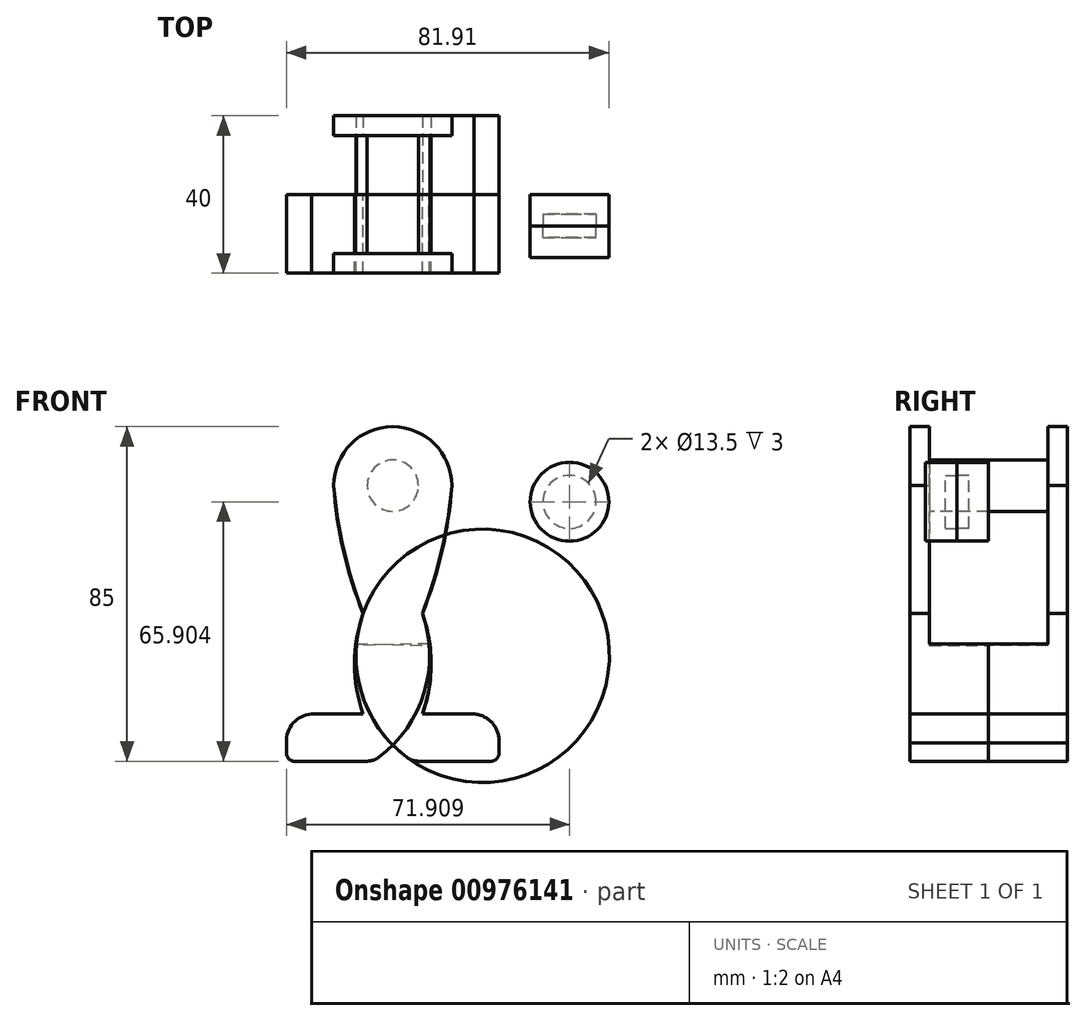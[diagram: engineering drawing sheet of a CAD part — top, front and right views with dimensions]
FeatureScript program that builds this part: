
annotation { "Feature Type Name" : "Feature", "Feature Type Description" : "" }
export const myFeature = defineFeature(function(context is Context, id is Id, definition is map)
    precondition{}
    {
        {
            var Q0;
            Q0=qCreatedBy(makeId("Front.planeOp"),FACE);
            var sketch = newSketch(context, id + "F0", { "sketchPlane" : qUnion([Q0])});
            skArc(sketch, "E0", {"start": v(14.72, 5.88) * mm, "mid": v(0.24, 23.76) * mm, "end": v(-14.8, 6.36) * mm});
            skLineSegment(sketch, "E1", {"start": v(-6.58, -61.23) * mm, "end": v(-25, -61.23) * mm});
            skPoint(sketch, "E2.visualSharp", {"position": v(0, -61.23) * mm});
            skLineSegment(sketch, "E3", {"start": v(-27, -59.23) * mm, "end": v(-27, -56.54) * mm});
            skLineSegment(sketch, "E4", {"start": v(-20.6, -49.23) * mm, "end": v(-7.5, -49.23) * mm});
            skArc(sketch, "E5", {"start": v(-15, 8.77) * mm, "mid": v(-12.53, -7.78) * mm, "end": v(-7.5, -23.73) * mm});
            skArc(sketch, "E6", {"start": v(7.5, -23.73) * mm, "mid": v(12.4, -7.75) * mm, "end": v(15, 8.77) * mm});
            skArc(sketch, "E7", {"start": v(-7.5, -23.73) * mm, "mid": v(-9.76, -36.48) * mm, "end": v(-7.5, -49.23) * mm});
            skArc(sketch, "E8", {"start": v(-3.6, -60.24) * mm, "mid": v(7.95, -43.8) * mm, "end": v(7.5, -23.73) * mm});
            skPoint(sketch, "E9.orphan", {"position": v(0, -23.73) * mm});
            skPoint(sketch, "E10.start.orphan", {"position": v(6, -49.23) * mm});
            skPoint(sketch, "E2.filletArc.end.orphan", {"position": v(0, -56.23) * mm});
            skPoint(sketch, "E11.visualSharp", {"position": v(-5, -61.23) * mm});
            skArc(sketch, "E11.filletArc", {"start": v(-6.58, -61.23) * mm, "mid": v(-5, -60.98) * mm, "end": v(-3.6, -60.24) * mm});
            skPoint(sketch, "E12.visualSharp", {"position": v(-27, -61.23) * mm});
            skArc(sketch, "E12.filletArc", {"start": v(-27, -59.23) * mm, "mid": v(-26.41, -60.65) * mm, "end": v(-25, -61.23) * mm});
            skPoint(sketch, "E13.visualSharp", {"position": v(-27, -49.23) * mm});
            skArc(sketch, "E14", {"start": v(-19.7, -49.23) * mm, "mid": v(-25, -51.23) * mm, "end": v(-27, -56.54) * mm});
            skPoint(sketch, "E15.orphan", {"position": v(-22, -54.23) * mm});
            skPoint(sketch, "E16.end.orphan", {"position": v(-18.3, -57.94) * mm});
            skSolve(sketch);
        }
        {
            var Q0;
            Q0=makeQuery(id+"F0.imprint","IMPRINT",FACE,{"disambiguationData":[TD([[makeQuery(id+"F0.imprint","IMPRINT",EDGE,{"derivedFrom":sQuery(id+"F0.wireOp",EDGE,"E1")}),-1.0]])]});
            extrude(context, id + "F1", {"entities" : qUnion([Q0]), "depth" : 20 * mm, "offsetDistance" : 25 * mm});
        }
        {
            var Q0;
            Q0=makeQuery(id+"F1.opExtrude","CAP_FACE",FACE,{"disambiguationData":[OSD([sQuery(id+"F0.wireOp",EDGE,"E0"),sQuery(id+"F0.wireOp",EDGE,"E1"),sQuery(id+"F0.wireOp",EDGE,"E3"),sQuery(id+"F0.wireOp",EDGE,"E4"),sQuery(id+"F0.wireOp",EDGE,"E5"),sQuery(id+"F0.wireOp",EDGE,"E6"),sQuery(id+"F0.wireOp",EDGE,"E7"),sQuery(id+"F0.wireOp",EDGE,"E8"),sQuery(id+"F0.wireOp",EDGE,"E11.filletArc"),sQuery(id+"F0.wireOp",EDGE,"E12.filletArc"),sQuery(id+"F0.wireOp",EDGE,"E14")])],"isStart":true});
            var sketch = newSketch(context, id + "F2", { "sketchPlane" : qUnion([Q0])});
            skLineSegment(sketch, "E17", {"start": v(0.76, 23.77) * mm, "end": v(-0.44, 23.77) * mm});
            skPoint(sketch, "E17.startSnap0", {"position": v(0, 23.77) * mm});
            skLineSegment(sketch, "E18", {"start": v(-15, 9.2) * mm, "end": v(-15, 8.77) * mm});
            skLineSegment(sketch, "E19", {"start": v(15, 9.53) * mm, "end": v(15, 8.77) * mm});
            skLineSegment(sketch, "E20", {"start": v(9.4, -31.38) * mm, "end": v(-9.23, -31.87) * mm});
            skArc(sketch, "E21", {"start": v(-15, 8.77) * mm, "mid": v(-12.5, -7.77) * mm, "end": v(-7.5, -23.73) * mm});
            skArc(sketch, "E22", {"start": v(7.5, -23.73) * mm, "mid": v(12.66, -7.81) * mm, "end": v(15, 8.77) * mm});
            skArc(sketch, "E23", {"start": v(-7.5, -23.73) * mm, "mid": v(-8.72, -27.72) * mm, "end": v(-9.23, -31.87) * mm});
            skArc(sketch, "E24", {"start": v(9.4, -31.38) * mm, "mid": v(8.77, -27.48) * mm, "end": v(7.5, -23.73) * mm});
            skArc(sketch, "E25", {"start": v(15, 8.77) * mm, "mid": v(10.72, 19.49) * mm, "end": v(0, 23.77) * mm});
            skArc(sketch, "E26", {"start": v(0, 23.77) * mm, "mid": v(-10.67, 19.44) * mm, "end": v(-15, 8.77) * mm});
            skPoint(sketch, "E27.orphan", {"position": v(15, 23.77) * mm});
            skSolve(sketch);
        }
        {
            var Q0;
            {var subQ7=sQuery(id+"F2.wireOp",EDGE,"E20");Q0=makeQuery(id+"F2.imprint","IMPRINT",FACE,{"disambiguationData":[TD([[makeQuery(id+"F2.imprint","IMPRINT",EDGE,{"derivedFrom":subQ7}),-1.0]])]});}
            extrude(context, id + "F3", {"entities" : qUnion([Q0]), "operationType" : NewBodyOperationType.REMOVE, "oppositeDirection" : true, "depth" : 15 * mm, "offsetDistance" : 25 * mm});
        }
        {
            var Q0;
            Q0=makeQuery(id+"F3.boolean.opBoolean","COPY",FACE,{"derivedFrom":makeQuery(id+"F3.opExtrude","CAP_FACE",FACE,{"disambiguationData":[OSD([sQuery(id+"F0.wireOp",EDGE,"E0"),sQuery(id+"F0.wireOp",EDGE,"E5"),sQuery(id+"F0.wireOp",EDGE,"E6"),sQuery(id+"F0.wireOp",EDGE,"E7"),sQuery(id+"F0.wireOp",EDGE,"E8"),sQuery(id+"F2.wireOp",EDGE,"E20")])],"isStart":false})});
            var sketch = newSketch(context, id + "F4", { "sketchPlane" : qUnion([Q0])});
            skCircle(sketch, "E28", {"center": v(0, 8.77) * mm, "radius": 6.5 * mm});
            skSolve(sketch);
        }
        {
            var Q0;
            Q0=makeQuery(id+"F4.imprint","IMPRINT",FACE,{"disambiguationData":[TD([[makeQuery(id+"F4.imprint","IMPRINT",EDGE,{"derivedFrom":sQuery(id+"F4.wireOp",EDGE,"E28")}),1.0]])]});
            extrude(context, id + "F5", {"entities" : qUnion([Q0]), "operationType" : NewBodyOperationType.ADD, "depth" : 15 * mm, "offsetDistance" : 25 * mm});
        }
        {
            var Q0;
            Q0=qCreatedBy(makeId("Front.planeOp"),FACE);
            var sketch = newSketch(context, id + "F6", { "sketchPlane" : qUnion([Q0])});
            skCircle(sketch, "E29", {"center": v(44.9, 4.67) * mm, "radius": 10 * mm});
            skSolve(sketch);
        }
        {
            var Q0;
            Q0=makeQuery(id+"F6.imprint","IMPRINT",FACE,{"disambiguationData":[TD([[makeQuery(id+"F6.imprint","IMPRINT",EDGE,{"derivedFrom":sQuery(id+"F6.wireOp",EDGE,"E29")}),1.0]])]});
            extrude(context, id + "F7", {"entities" : qUnion([Q0]), "depth" : 8 * mm, "offsetDistance" : 25 * mm});
        }
        {
            var Q0;
            Q0=makeQuery(id+"F7.opExtrude","CAP_FACE",FACE,{"disambiguationData":[OSD([sQuery(id+"F6.wireOp",EDGE,"E29")])],"isStart":false});
            var sketch = newSketch(context, id + "F8", { "sketchPlane" : qUnion([Q0])});
            skCircle(sketch, "E30", {"center": v(44.9, 4.67) * mm, "radius": 6.75 * mm});
            skSolve(sketch);
        }
        {
            var Q0;
            Q0 = qSketchRegion(id + "F8", true);
            extrude(context, id + "F9", {"entities" : qUnion([Q0]), "operationType" : NewBodyOperationType.REMOVE, "oppositeDirection" : true, "depth" : 3 * mm, "offsetDistance" : 25 * mm});
        }
        {
            var Q0;
            Q0=makeQuery(id+"F1.opExtrude","SWEPT_BODY",BODY,{"disambiguationData":[OSD([sQuery(id+"F0.wireOp",EDGE,"E0"),sQuery(id+"F0.wireOp",EDGE,"E1"),sQuery(id+"F0.wireOp",EDGE,"E3"),sQuery(id+"F0.wireOp",EDGE,"E4"),sQuery(id+"F0.wireOp",EDGE,"E5"),sQuery(id+"F0.wireOp",EDGE,"E6"),sQuery(id+"F0.wireOp",EDGE,"E7"),sQuery(id+"F0.wireOp",EDGE,"E8"),sQuery(id+"F0.wireOp",EDGE,"E11.filletArc"),sQuery(id+"F0.wireOp",EDGE,"E12.filletArc"),sQuery(id+"F0.wireOp",EDGE,"E14")])]});
            var Q1;
            Q1=qCreatedBy(makeId("Right.planeOp"),FACE);
            mirror(context, id + "F10", {"entities" : qUnion([Q0]), "mirrorPlane" : qUnion([Q1])});
        }
        {
            var Q0;
            Q0=makeQuery(id+"F10.opPattern","COPY",BODY,{"derivedFrom":makeQuery(id+"F1.opExtrude","SWEPT_BODY",BODY,{"disambiguationData":[OSD([sQuery(id+"F0.wireOp",EDGE,"E0"),sQuery(id+"F0.wireOp",EDGE,"E1"),sQuery(id+"F0.wireOp",EDGE,"E3"),sQuery(id+"F0.wireOp",EDGE,"E4"),sQuery(id+"F0.wireOp",EDGE,"E5"),sQuery(id+"F0.wireOp",EDGE,"E6"),sQuery(id+"F0.wireOp",EDGE,"E7"),sQuery(id+"F0.wireOp",EDGE,"E8"),sQuery(id+"F0.wireOp",EDGE,"E11.filletArc"),sQuery(id+"F0.wireOp",EDGE,"E12.filletArc"),sQuery(id+"F0.wireOp",EDGE,"E14")])]}),"instanceName":"1"});
            var Q1;
            Q1=makeQuery(id+"F10.opPattern","COPY",FACE,{"derivedFrom":makeQuery(id+"F5.opExtrude","CAP_FACE",FACE,{"disambiguationData":[OSD([sQuery(id+"F4.wireOp",EDGE,"E28")])],"isStart":false}),"instanceName":"1"});
            mirror(context, id + "F11", {"entities" : qUnion([Q0]), "mirrorPlane" : qUnion([Q1])});
        }
        {
            var Q0;
            Q0=makeQuery(id+"F7.opExtrude","SWEPT_BODY",BODY,{"disambiguationData":[OSD([sQuery(id+"F6.wireOp",EDGE,"E29")])]});
            var Q1;
            Q1=makeQuery(id+"F7.opExtrude","CAP_FACE",FACE,{"disambiguationData":[OSD([sQuery(id+"F6.wireOp",EDGE,"E29")])],"isStart":false});
            mirror(context, id + "F12", {"entities" : qUnion([Q0]), "mirrorPlane" : qUnion([Q1])});
        }
    });
